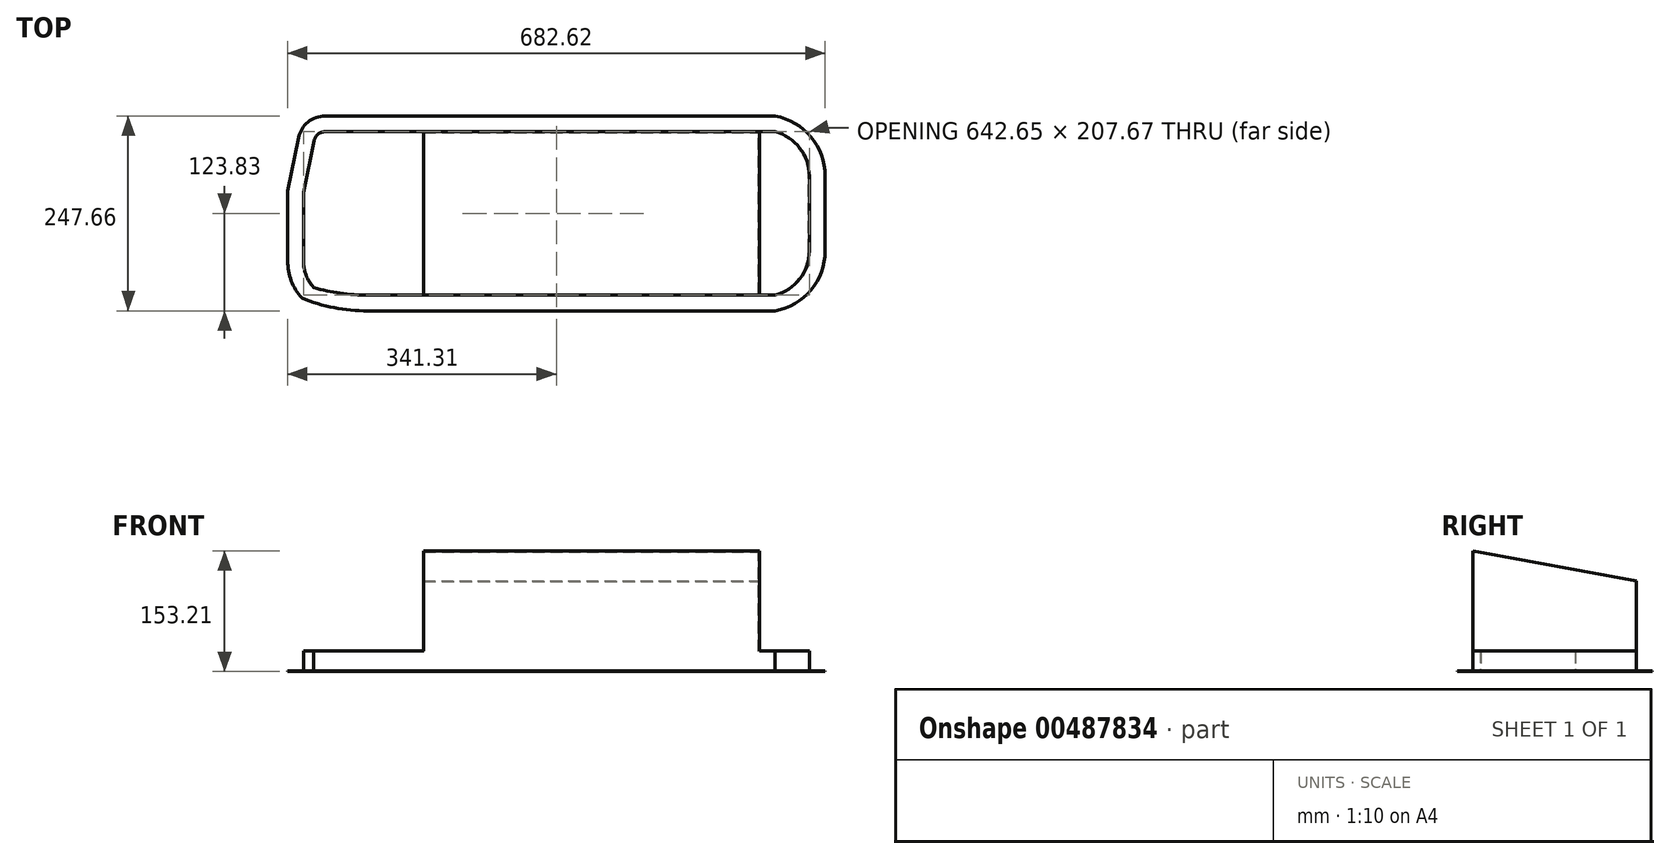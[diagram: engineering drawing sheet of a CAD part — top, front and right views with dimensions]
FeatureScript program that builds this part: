
annotation { "Feature Type Name" : "Feature", "Feature Type Description" : "" }
export const myFeature = defineFeature(function(context is Context, id is Id, definition is map)
    precondition{}
    {
        {
            var Q0;
            Q0=qCreatedBy(makeId("Top.planeOp"),FACE);
            var sketch = newSketch(context, id + "F0", { "sketchPlane" : qUnion([Q0])});
            skLineSegment(sketch, "E0.bottom", {"start": v(-341.31, 123.82) * mm, "end": v(341.31, 123.82) * mm});
            skLineSegment(sketch, "E0.top", {"start": v(-341.31, -123.83) * mm, "end": v(341.31, -123.83) * mm});
            skLineSegment(sketch, "E0.left", {"start": v(-341.31, 123.82) * mm, "end": v(-341.31, -123.83) * mm});
            skLineSegment(sketch, "E0.right", {"start": v(341.31, 123.83) * mm, "end": v(341.31, -123.83) * mm});
            skLineSegment(sketch, "E1", {"start": v(-341.31, 123.82) * mm, "end": v(-341.31, 84.93) * mm});
            skLineSegment(sketch, "E2", {"start": v(-341.31, 123.82) * mm, "end": v(-341.31, 28.58) * mm});
            skLineSegment(sketch, "E3", {"start": v(-341.31, 123.82) * mm, "end": v(-293.69, 123.82) * mm});
            skArc(sketch, "E4", {"start": v(-293.69, 123.82) * mm, "mid": v(-315.44, 116.08) * mm, "end": v(-327.4, 96.32) * mm});
            skLineSegment(sketch, "E5", {"start": v(-341.31, 28.57) * mm, "end": v(-327.4, 96.32) * mm});
            skPoint(sketch, "E6.orphan", {"position": v(-327.82, 84.93) * mm});
            skLineSegment(sketch, "E7", {"start": v(-341.31, -123.83) * mm, "end": v(-341.31, -60.33) * mm});
            skLineSegment(sketch, "E8", {"start": v(-341.31, -123.83) * mm, "end": v(-239.71, -123.83) * mm});
            skArc(sketch, "E9", {"start": v(-341.31, -60.33) * mm, "mid": v(-336.63, -85.61) * mm, "end": v(-323.2, -107.55) * mm});
            skArc(sketch, "E10", {"start": v(-323.2, -107.55) * mm, "mid": v(-282.25, -119.72) * mm, "end": v(-239.71, -123.83) * mm});
            skLineSegment(sketch, "E11", {"start": v(-341.31, -123.83) * mm, "end": v(-270.67, -60.33) * mm});
            skLineSegment(sketch, "E12", {"start": v(341.31, 123.82) * mm, "end": v(277.81, 123.82) * mm});
            skLineSegment(sketch, "E13", {"start": v(341.31, 123.82) * mm, "end": v(341.31, 47.62) * mm});
            skArc(sketch, "E14", {"start": v(341.31, 47.62) * mm, "mid": v(323.36, 97.22) * mm, "end": v(277.81, 123.83) * mm});
            skLineSegment(sketch, "E15", {"start": v(341.31, -123.83) * mm, "end": v(341.31, -47.63) * mm});
            skLineSegment(sketch, "E16", {"start": v(341.31, -123.83) * mm, "end": v(277.81, -123.83) * mm});
            skLineSegment(sketch, "E17", {"start": v(277.81, 123.82) * mm, "end": v(277.81, 103.84) * mm});
            skLineSegment(sketch, "E18", {"start": v(277.81, 103.84) * mm, "end": v(-293.69, 103.84) * mm});
            skLineSegment(sketch, "E19", {"start": v(-293.69, 123.82) * mm, "end": v(-293.69, 89.4) * mm});
            skLineSegment(sketch, "E20", {"start": v(-334.36, 62.45) * mm, "end": v(-314.78, 58.43) * mm});
            skLineSegment(sketch, "E21", {"start": v(-314.78, 58.43) * mm, "end": v(-307.83, 92.3) * mm});
            skLineSegment(sketch, "E22", {"start": v(-327.4, 96.32) * mm, "end": v(-293.69, 89.4) * mm});
            skArc(sketch, "E23", {"start": v(-293.69, 103.84) * mm, "mid": v(-302.8, 100.59) * mm, "end": v(-307.83, 92.3) * mm});
            skLineSegment(sketch, "E24", {"start": v(-314.78, 58.43) * mm, "end": v(-321.32, 26.54) * mm});
            skLineSegment(sketch, "E25", {"start": v(-341.31, -60.33) * mm, "end": v(-321.32, -60.33) * mm});
            skLineSegment(sketch, "E26", {"start": v(-321.32, -60.33) * mm, "end": v(-321.32, 26.54) * mm});
            skLineSegment(sketch, "E27", {"start": v(-323.2, -107.55) * mm, "end": v(-308.34, -94.19) * mm});
            skArc(sketch, "E28", {"start": v(-321.32, -60.33) * mm, "mid": v(-317.97, -78.46) * mm, "end": v(-308.34, -94.19) * mm});
            skLineSegment(sketch, "E29", {"start": v(-239.71, -123.83) * mm, "end": v(-239.71, -103.84) * mm});
            skLineSegment(sketch, "E30", {"start": v(-239.71, -103.84) * mm, "end": v(-214.31, -103.84) * mm});
            skArc(sketch, "E31", {"start": v(-308.34, -94.19) * mm, "mid": v(-274.36, -101.41) * mm, "end": v(-239.71, -103.84) * mm});
            skLineSegment(sketch, "E32", {"start": v(-239.71, -103.84) * mm, "end": v(277.81, -103.84) * mm});
            skLineSegment(sketch, "E33", {"start": v(277.81, -123.83) * mm, "end": v(277.81, -103.84) * mm});
            skLineSegment(sketch, "E34", {"start": v(341.31, -47.63) * mm, "end": v(321.32, -47.63) * mm});
            skLineSegment(sketch, "E35", {"start": v(321.32, -47.63) * mm, "end": v(321.32, -22.23) * mm});
            skArc(sketch, "E36", {"start": v(277.81, -123.83) * mm, "mid": v(323.36, -97.22) * mm, "end": v(341.31, -47.63) * mm});
            skArc(sketch, "E37", {"start": v(277.81, -103.84) * mm, "mid": v(309.17, -83.17) * mm, "end": v(321.32, -47.63) * mm});
            skLineSegment(sketch, "E38", {"start": v(321.32, -22.23) * mm, "end": v(321.32, 47.62) * mm});
            skPoint(sketch, "E38.endSnap0", {"position": v(321.32, -34.93) * mm});
            skLineSegment(sketch, "E39", {"start": v(341.31, 47.62) * mm, "end": v(321.32, 47.62) * mm});
            skPoint(sketch, "E40.orphan", {"position": v(321.32, 83.22) * mm});
            skArc(sketch, "E41", {"start": v(321.32, 47.62) * mm, "mid": v(309.17, 83.17) * mm, "end": v(277.81, 103.84) * mm});
            skLineSegment(sketch, "E42", {"start": v(-341.31, 0) * mm, "end": v(341.31, 0) * mm});
            skLineSegment(sketch, "E43", {"start": v(0, 123.83) * mm, "end": v(0, -123.83) * mm});
            skLineSegment(sketch, "E44", {"start": v(0, 0) * mm, "end": v(341.31, 0) * mm});
            skSolve(sketch);
        }
        {
            var Q0;
            {var subQ1=sQuery(id+"F0.wireOp",EDGE,"E0.bottom");var subQ3=sQuery(id+"F0.wireOp",EDGE,"E43");var subQ4=makeQuery(id+"F0.imprint","INTERSECT",VERTEX,{"derivedFrom":[subQ1,subQ3]});Q0=makeQuery(id+"F0.imprint","IMPRINT",FACE,{"disambiguationData":[TD([[makeQuery(id+"F0.imprint","IMPRINT",EDGE,{"disambiguationData":[TD([[subQ4,-1.0]])],"derivedFrom":subQ3}),-1.0]])]});}
            var Q1;
            {var subQ0=sQuery(id+"F0.wireOp",EDGE,"E4");Q1=makeQuery(id+"F0.imprint","IMPRINT",FACE,{"disambiguationData":[TD([[makeQuery(id+"F0.imprint","IMPRINT",EDGE,{"derivedFrom":subQ0}),1.0]])]});}
            var Q2;
            {var subQ3=sQuery(id+"F0.wireOp",EDGE,"E20");Q2=makeQuery(id+"F0.imprint","IMPRINT",FACE,{"disambiguationData":[TD([[makeQuery(id+"F0.imprint","IMPRINT",EDGE,{"derivedFrom":subQ3}),1.0]])]});}
            var Q3;
            {var subQ4=sQuery(id+"F0.wireOp",EDGE,"E20");Q3=makeQuery(id+"F0.imprint","IMPRINT",FACE,{"disambiguationData":[TD([[makeQuery(id+"F0.imprint","IMPRINT",EDGE,{"derivedFrom":subQ4}),-1.0]])]});}
            var Q4;
            {var subQ0=sQuery(id+"F0.wireOp",EDGE,"E25");Q4=makeQuery(id+"F0.imprint","IMPRINT",FACE,{"disambiguationData":[TD([[makeQuery(id+"F0.imprint","IMPRINT",EDGE,{"derivedFrom":subQ0}),1.0]])]});}
            var Q5;
            Q5=makeQuery(id+"F0.imprint","IMPRINT",FACE,{"disambiguationData":[TD([[makeQuery(id+"F0.imprint","IMPRINT",EDGE,{"derivedFrom":sQuery(id+"F0.wireOp",EDGE,"E9")}),1.0]])]});
            var Q6;
            Q6=makeQuery(id+"F0.imprint","IMPRINT",FACE,{"disambiguationData":[TD([[makeQuery(id+"F0.imprint","IMPRINT",EDGE,{"derivedFrom":sQuery(id+"F0.wireOp",EDGE,"E10")}),1.0]])]});
            var Q7;
            {var subQ1=sQuery(id+"F0.wireOp",EDGE,"E29");Q7=makeQuery(id+"F0.imprint","IMPRINT",FACE,{"disambiguationData":[TD([[makeQuery(id+"F0.imprint","IMPRINT",EDGE,{"derivedFrom":subQ1}),-1.0]])]});}
            var Q8;
            Q8=makeQuery(id+"F0.imprint","IMPRINT",FACE,{"disambiguationData":[TD([[makeQuery(id+"F0.imprint","IMPRINT",EDGE,{"derivedFrom":sQuery(id+"F0.wireOp",EDGE,"E33")}),-1.0]])]});
            var Q9;
            {var subQ0=sQuery(id+"F0.wireOp",EDGE,"E33");Q9=makeQuery(id+"F0.imprint","IMPRINT",FACE,{"disambiguationData":[TD([[makeQuery(id+"F0.imprint","IMPRINT",EDGE,{"derivedFrom":subQ0}),1.0]])]});}
            var Q10;
            {var subQ6=sQuery(id+"F0.wireOp",EDGE,"E34");Q10=makeQuery(id+"F0.imprint","IMPRINT",FACE,{"disambiguationData":[TD([[makeQuery(id+"F0.imprint","IMPRINT",EDGE,{"derivedFrom":subQ6}),-1.0]])]});}
            var Q11;
            {var subQ0=sQuery(id+"F0.wireOp",EDGE,"E39");Q11=makeQuery(id+"F0.imprint","IMPRINT",FACE,{"disambiguationData":[TD([[makeQuery(id+"F0.imprint","IMPRINT",EDGE,{"derivedFrom":subQ0}),1.0]])]});}
            var Q12;
            Q12=makeQuery(id+"F0.imprint","IMPRINT",FACE,{"disambiguationData":[TD([[makeQuery(id+"F0.imprint","IMPRINT",EDGE,{"derivedFrom":sQuery(id+"F0.wireOp",EDGE,"E14")}),1.0]])]});
            var Q13;
            {var subQ0=sQuery(id+"F0.wireOp",EDGE,"E17");Q13=makeQuery(id+"F0.imprint","IMPRINT",FACE,{"disambiguationData":[TD([[makeQuery(id+"F0.imprint","IMPRINT",EDGE,{"derivedFrom":subQ0}),-1.0]])]});}
            extrude(context, id + "F1", {"entities" : qUnion([Q0, Q1, Q2, Q3, Q4, Q5, Q6, Q7, Q8, Q9, Q10, Q11, Q12, Q13]), "depth" : 0.81 * mm});
        }
        {
            var Q0;
            Q0=makeQuery(id+"F1.opExtrude","CAP_FACE",FACE,{"disambiguationData":[OSD([sQuery(id+"F0.wireOp",EDGE,"E0.bottom"),sQuery(id+"F0.wireOp",EDGE,"E0.top"),sQuery(id+"F0.wireOp",EDGE,"E0.left"),sQuery(id+"F0.wireOp",EDGE,"E0.right"),sQuery(id+"F0.wireOp",EDGE,"E4"),sQuery(id+"F0.wireOp",EDGE,"E5"),sQuery(id+"F0.wireOp",EDGE,"E9"),sQuery(id+"F0.wireOp",EDGE,"E10"),sQuery(id+"F0.wireOp",EDGE,"E14"),sQuery(id+"F0.wireOp",EDGE,"E18"),sQuery(id+"F0.wireOp",EDGE,"E21"),sQuery(id+"F0.wireOp",EDGE,"E23"),sQuery(id+"F0.wireOp",EDGE,"E24"),sQuery(id+"F0.wireOp",EDGE,"E26"),sQuery(id+"F0.wireOp",EDGE,"E28"),sQuery(id+"F0.wireOp",EDGE,"E31"),sQuery(id+"F0.wireOp",EDGE,"E32"),sQuery(id+"F0.wireOp",EDGE,"E35"),sQuery(id+"F0.wireOp",EDGE,"E36"),sQuery(id+"F0.wireOp",EDGE,"E37"),sQuery(id+"F0.wireOp",EDGE,"E38"),sQuery(id+"F0.wireOp",EDGE,"E41")])],"isStart":false});
            var sketch = newSketch(context, id + "F2", { "sketchPlane" : qUnion([Q0])});
            skLineSegment(sketch, "E45.0", {"start": v(277.81, 103.84) * mm, "end": v(-293.69, 103.84) * mm});
            skArc(sketch, "E46.0", {"start": v(-293.69, 103.84) * mm, "mid": v(-302.8, 100.59) * mm, "end": v(-307.83, 92.3) * mm});
            skLineSegment(sketch, "E47.0", {"start": v(-321.32, 26.54) * mm, "end": v(-307.83, 92.3) * mm});
            skLineSegment(sketch, "E48.0", {"start": v(-321.32, -60.33) * mm, "end": v(-321.32, 26.54) * mm});
            skArc(sketch, "E49.0", {"start": v(-321.32, -60.33) * mm, "mid": v(-317.97, -78.46) * mm, "end": v(-308.34, -94.19) * mm});
            skArc(sketch, "E50.0", {"start": v(-308.34, -94.19) * mm, "mid": v(-274.36, -101.41) * mm, "end": v(-239.71, -103.84) * mm});
            skLineSegment(sketch, "E51.0", {"start": v(-239.71, -103.84) * mm, "end": v(277.81, -103.84) * mm});
            skArc(sketch, "E52.0", {"start": v(277.81, -103.84) * mm, "mid": v(309.17, -83.17) * mm, "end": v(321.32, -47.63) * mm});
            skLineSegment(sketch, "E53.0", {"start": v(321.32, -47.63) * mm, "end": v(321.32, 47.62) * mm});
            skArc(sketch, "E54.0", {"start": v(321.32, 47.62) * mm, "mid": v(309.17, 83.17) * mm, "end": v(277.81, 103.84) * mm});
            skSolve(sketch);
        }
        {
            var Q0;
            Q0 = qSketchRegion(id + "F2", true);
            extrude(context, id + "F3", {"entities" : qUnion([Q0]), "depth" : 152.4 * mm, "offsetDistance" : 25.4 * mm});
        }
        {
            var Q0;
            Q0=makeQuery(id+"F3.opExtrude","CAP_FACE",FACE,{"disambiguationData":[OSD([sQuery(id+"F2.wireOp",EDGE,"E45.0"),sQuery(id+"F2.wireOp",EDGE,"E46.0"),sQuery(id+"F2.wireOp",EDGE,"E47.0"),sQuery(id+"F2.wireOp",EDGE,"E48.0"),sQuery(id+"F2.wireOp",EDGE,"E49.0"),sQuery(id+"F2.wireOp",EDGE,"E50.0"),sQuery(id+"F2.wireOp",EDGE,"E51.0"),sQuery(id+"F2.wireOp",EDGE,"E52.0"),sQuery(id+"F2.wireOp",EDGE,"E53.0"),sQuery(id+"F2.wireOp",EDGE,"E54.0")])],"isStart":false});
            var sketch = newSketch(context, id + "F4", { "sketchPlane" : qUnion([Q0])});
            skLineSegment(sketch, "E55", {"start": v(-168.92, 103.84) * mm, "end": v(-168.92, -103.84) * mm});
            skLineSegment(sketch, "E56.0", {"start": v(-239.71, -103.84) * mm, "end": v(-168.92, -103.84) * mm});
            skArc(sketch, "E57.0", {"start": v(-308.34, -94.19) * mm, "mid": v(-274.36, -101.41) * mm, "end": v(-239.71, -103.84) * mm});
            skArc(sketch, "E58.0", {"start": v(-321.32, -60.33) * mm, "mid": v(-317.97, -78.46) * mm, "end": v(-308.34, -94.19) * mm});
            skLineSegment(sketch, "E59.0", {"start": v(-321.32, -60.33) * mm, "end": v(-321.32, 26.54) * mm});
            skLineSegment(sketch, "E60.0", {"start": v(-321.32, 26.54) * mm, "end": v(-307.83, 92.3) * mm});
            skPoint(sketch, "E61.0", {"position": v(-302.8, 100.59) * mm});
            skLineSegment(sketch, "E62.0", {"start": v(-168.92, 103.84) * mm, "end": v(-293.69, 103.84) * mm});
            skArc(sketch, "E63.0", {"start": v(-293.69, 103.84) * mm, "mid": v(-302.8, 100.59) * mm, "end": v(-307.83, 92.3) * mm});
            skPoint(sketch, "E64.orphan", {"position": v(277.81, 103.84) * mm});
            skPoint(sketch, "E65.orphan", {"position": v(277.81, -103.84) * mm});
            skSolve(sketch);
        }
        {
            var Q0;
            Q0 = qSketchRegion(id + "F4", true);
            extrude(context, id + "F5", {"entities" : qUnion([Q0]), "operationType" : NewBodyOperationType.REMOVE, "oppositeDirection" : true, "depth" : 127 * mm, "offsetDistance" : 25.4 * mm});
        }
        {
            var Q0;
            Q0=makeQuery(id+"F3.opExtrude","CAP_FACE",FACE,{"disambiguationData":[OSD([sQuery(id+"F2.wireOp",EDGE,"E45.0"),sQuery(id+"F2.wireOp",EDGE,"E46.0"),sQuery(id+"F2.wireOp",EDGE,"E47.0"),sQuery(id+"F2.wireOp",EDGE,"E48.0"),sQuery(id+"F2.wireOp",EDGE,"E49.0"),sQuery(id+"F2.wireOp",EDGE,"E50.0"),sQuery(id+"F2.wireOp",EDGE,"E51.0"),sQuery(id+"F2.wireOp",EDGE,"E52.0"),sQuery(id+"F2.wireOp",EDGE,"E53.0"),sQuery(id+"F2.wireOp",EDGE,"E54.0")])],"isStart":false});
            var sketch = newSketch(context, id + "F6", { "sketchPlane" : qUnion([Q0])});
            skLineSegment(sketch, "E66.0", {"start": v(-168.92, -103.84) * mm, "end": v(277.81, -103.84) * mm});
            skArc(sketch, "E67.0", {"start": v(277.81, -103.84) * mm, "mid": v(309.17, -83.17) * mm, "end": v(321.32, -47.63) * mm});
            skLineSegment(sketch, "E68.0", {"start": v(321.32, -47.63) * mm, "end": v(321.32, 47.62) * mm});
            skArc(sketch, "E69.0", {"start": v(321.32, 47.62) * mm, "mid": v(309.17, 83.17) * mm, "end": v(277.81, 103.84) * mm});
            skLineSegment(sketch, "E70.0", {"start": v(277.81, 103.84) * mm, "end": v(-168.92, 103.84) * mm});
            skLineSegment(sketch, "E71", {"start": v(257.82, -103.84) * mm, "end": v(257.82, 103.84) * mm});
            skSolve(sketch);
        }
        {
            var Q0;
            Q0 = qSketchRegion(id + "F6", true);
            extrude(context, id + "F7", {"entities" : qUnion([Q0]), "operationType" : NewBodyOperationType.REMOVE, "oppositeDirection" : true, "depth" : 127 * mm, "offsetDistance" : 25.4 * mm});
        }
        {
            var Q0;
            Q0=makeQuery(id+"F7.boolean.opBoolean","COPY",FACE,{"derivedFrom":makeQuery(id+"F7.opExtrude","SWEPT_FACE",FACE,{"disambiguationData":[OSD([sQuery(id+"F6.wireOp",EDGE,"E71")])]})});
            var sketch = newSketch(context, id + "F8", { "sketchPlane" : qUnion([Q0])});
            skLineSegment(sketch, "E72", {"start": v(-103.84, 153.21) * mm, "end": v(103.84, 115.11) * mm});
            skLineSegment(sketch, "E73.0", {"start": v(103.84, 115.11) * mm, "end": v(103.84, 153.21) * mm});
            skLineSegment(sketch, "E74.0", {"start": v(-103.84, 26.21) * mm, "end": v(103.84, 26.21) * mm});
            skLineSegment(sketch, "E75.0", {"start": v(-103.84, 153.21) * mm, "end": v(103.84, 153.21) * mm});
            skSolve(sketch);
        }
        {
            var Q0;
            Q0 = qSketchRegion(id + "F8", true);
            extrude(context, id + "F9", {"entities" : qUnion([Q0]), "operationType" : NewBodyOperationType.REMOVE, "endBound" : BoundingType.THROUGH_ALL, "oppositeDirection" : true, "depth" : 25.4 * mm, "offsetDistance" : 25.4 * mm});
        }
        {
            var Q0;
            Q0=makeQuery(id+"F3.opExtrude","CAP_FACE",FACE,{"disambiguationData":[OSD([sQuery(id+"F2.wireOp",EDGE,"E45.0"),sQuery(id+"F2.wireOp",EDGE,"E46.0"),sQuery(id+"F2.wireOp",EDGE,"E47.0"),sQuery(id+"F2.wireOp",EDGE,"E48.0"),sQuery(id+"F2.wireOp",EDGE,"E49.0"),sQuery(id+"F2.wireOp",EDGE,"E50.0"),sQuery(id+"F2.wireOp",EDGE,"E51.0"),sQuery(id+"F2.wireOp",EDGE,"E52.0"),sQuery(id+"F2.wireOp",EDGE,"E53.0"),sQuery(id+"F2.wireOp",EDGE,"E54.0")])],"isStart":true});
            shell(context, id + "F10", {"entities" : qUnion([Q0]), "thickness" : 0.81 * mm});
        }
    });
